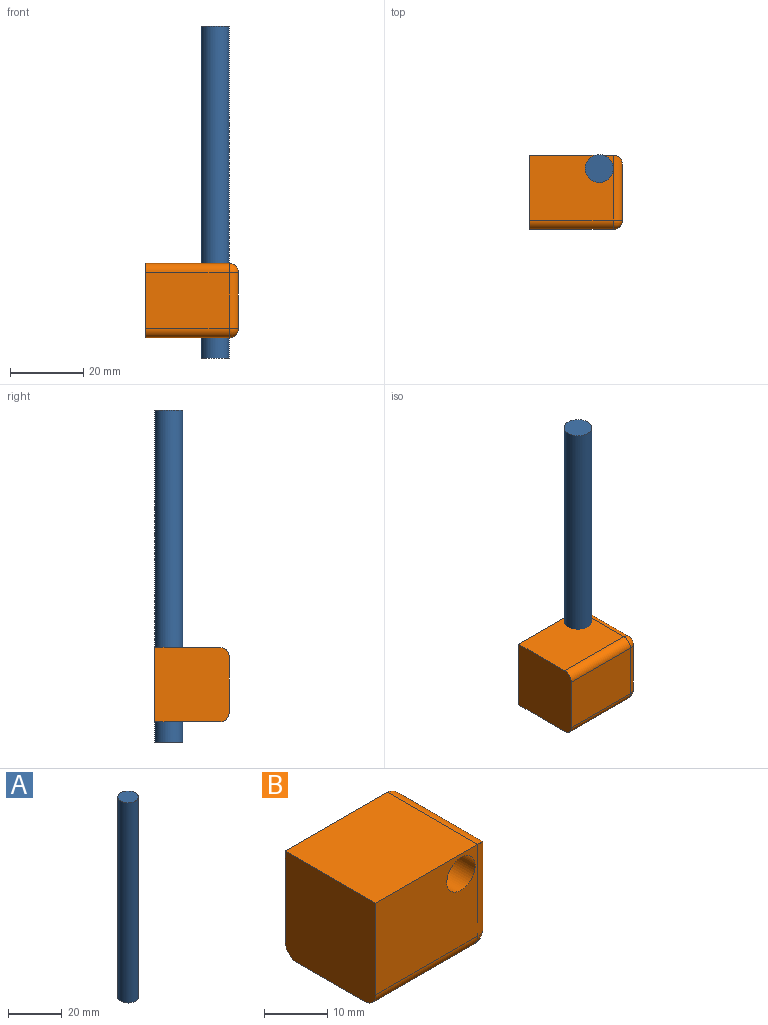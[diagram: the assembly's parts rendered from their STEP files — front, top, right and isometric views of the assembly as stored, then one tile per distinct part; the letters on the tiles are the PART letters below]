
ASSEMBLY  parts=2 mates=1
PART A: 3 faces, bbox 7.6x7.6x90.8 mm
  f0: cylinder r=3.81mm len=90.82mm, axis (0,0,-1), area 2174.2mm2, adj f1,f2
  f1: plane 7.62x7.62mm, normal (0,0,1), area 45.6mm2, adj f0
  f2: plane 7.62x7.62mm, normal (0,0,-1), area 45.6mm2, adj f0
PART B: 15 faces, bbox 25.4x20.3x20.3 mm
  f0: plane 22.86x17.78mm, normal (0,1,0), area 374.8mm2, adj f1,f5,f6,f7,f8
  f1: plane 22.86x20.32mm, normal (0,0,1), area 464.5mm2, adj f0,f2,f5,f9
  f2: plane 22.86x17.78mm, normal (0,-1,0), area 374.8mm2, adj f1,f5,f6,f11,f14
  f3: plane 22.86x15.24mm, normal (0,0,-1), area 348.4mm2, adj f5,f8,f12,f14
  f4: plane 15.24x15.24mm, normal (1,0,0), area 232.3mm2, adj f7,f9,f11,f12
  f5: plane 20.32x20.32mm, normal (-1,0,0), area 410.1mm2, adj f0,f1,f2,f3,f8,f14
  f6: cylinder r=3.17mm len=20.32mm, axis (0,1,0), area 405.4mm2, adj f0,f2
  f7: cylinder r=2.54mm len=17.78mm, axis (0,0,-1), area 67.3mm2, adj f0,f4,f9,f10
  f8: cylinder r=2.54mm len=22.86mm, axis (-1,0,0), area 91.2mm2, adj f0,f3,f5,f10
  f9: cylinder r=2.54mm len=20.32mm, axis (0,1,0), area 73.7mm2, adj f1,f4,f7,f11
  f10: sphere r=2.54mm, area 10.1mm2, adj f7,f8,f12
  f11: cylinder r=2.54mm len=17.78mm, axis (0,0,1), area 67.3mm2, adj f2,f4,f9,f13
  f12: cylinder r=2.54mm len=15.24mm, axis (0,-1,0), area 60.8mm2, adj f3,f4,f10,f13
  f13: sphere r=2.54mm, area 10.1mm2, adj f11,f12,f14
  f14: cylinder r=2.54mm len=22.86mm, axis (1,0,0), area 91.2mm2, adj f2,f3,f5,f13
PLACE A t=(-7.05,-18.04,-1.41)mm
PLACE B rot(axis=(-1,0,0),90deg) t=(-23.71,-31.58,24.45)mm
MATE cylindrical B.f6 <-> A.f0  axis (0,0,-1) through (-4.66,-15.07,24.45)mm
